# Revit family: 2059438 Lighting Fixture_Sylvania_Lytepanel II-Surface 1200x300_Surface Mounted
name_source: partatom
category: Lighting Fixtures
revit_build: Autodesk Revit 2017 (Build: 20190507_1515(x64)
units: mm (PartAtom-declared; Revit-internal decimal feet)

## family parameters
Cut with Voids When Loaded = No
Host = Face
Light Source = Yes
OmniClass Number = 23.80.70.11.17
OmniClass Title = Specialized Lighting by Location or Use
Part Type = Normal
Room Calculation Point = No
Round Connector Dimension = Use Diameter
Shared = No

## types (1)
- LYTEPANEL II 1200 4K DALI SM
    Apparent Load = 32 VA
    Assembly Code = D5020200
    Beam Angle = 120.00°
    Body Material = Steel_Sylvania_Lytepanel II_White
    CRI ( Ra ) = 80
    Catalog Number = 2059438 LYTEPANEL II 1200 4K DALI SM
    Color Filter = 16777215
    Default Elevation = 0 mm  [stored 0 ft]
    Description = Architectural flat panel with even homogenous light distribution. Lay-in for 600 x 600 & 1200 x 300 exposed T bar grid systems with SAS330/SAS330G versions available. Up to 4640 fixture lumens. Up to 145 lumens per watt effi ciency. Uses new highly transmissive LED diffuser material. Low glare version with UGR <18
    Diffuser Material = Polycarbonate_Sylvania_Lytepanel II_
    Dimming Lamp Color Temperature Shift = <None>
    Dimming Range = 1%-100%
    Drive Current = 275mA
    Electrical Protection = CLASS I
    Emit Shape Visible in Rendering = No
    Emit from Rectangle Length = 1140 mm
    Emit from Rectangle Width = 246 mm
    Energy Class = A++,A+, A
    Glare Control = UGR<18
    Glow Wire Test = 650 °C
    Height = 95 mm
    IK Rating = IK02
    IP Rating = IP40
    LOR = 100%
    Lamp = Integrated LED
    Length = 1260 mm  [stored 4.13386 ft]
    Life = 50 000h
    Manufacturer = Feilo Sylvania
    Model = LYTEPANEL II 1200 4K DALI SM
    Photometric Web File = 2059438_LYTEPANELII12004KDALISM-208806.ies
    Product Family = LYTEPANEL II SURFACE 1200x300
    Product Page URL = http://www.sylvania-lighting.com
    Reflector Material = Metal_Sylvania_Lytepanel II_Silver
    Tilt Angle = -90.00°
    URL = http://www.sylvania-lighting.com
    Voltage = 230 V
    Voltage Comments = UNI ( Universal Voltage; 220-240 Volt )
    Weight = 8.2 kg
    Width = 310 mm  [stored 1.01706 ft]

note: [stored X ft] marks values corroborated as IEEE doubles in the binary element streams (Revit-internal decimal feet)

## geometry (parser evidence)
native form markers: Blend x4, Sweep x2
no freeform markers — native parametric forms only
